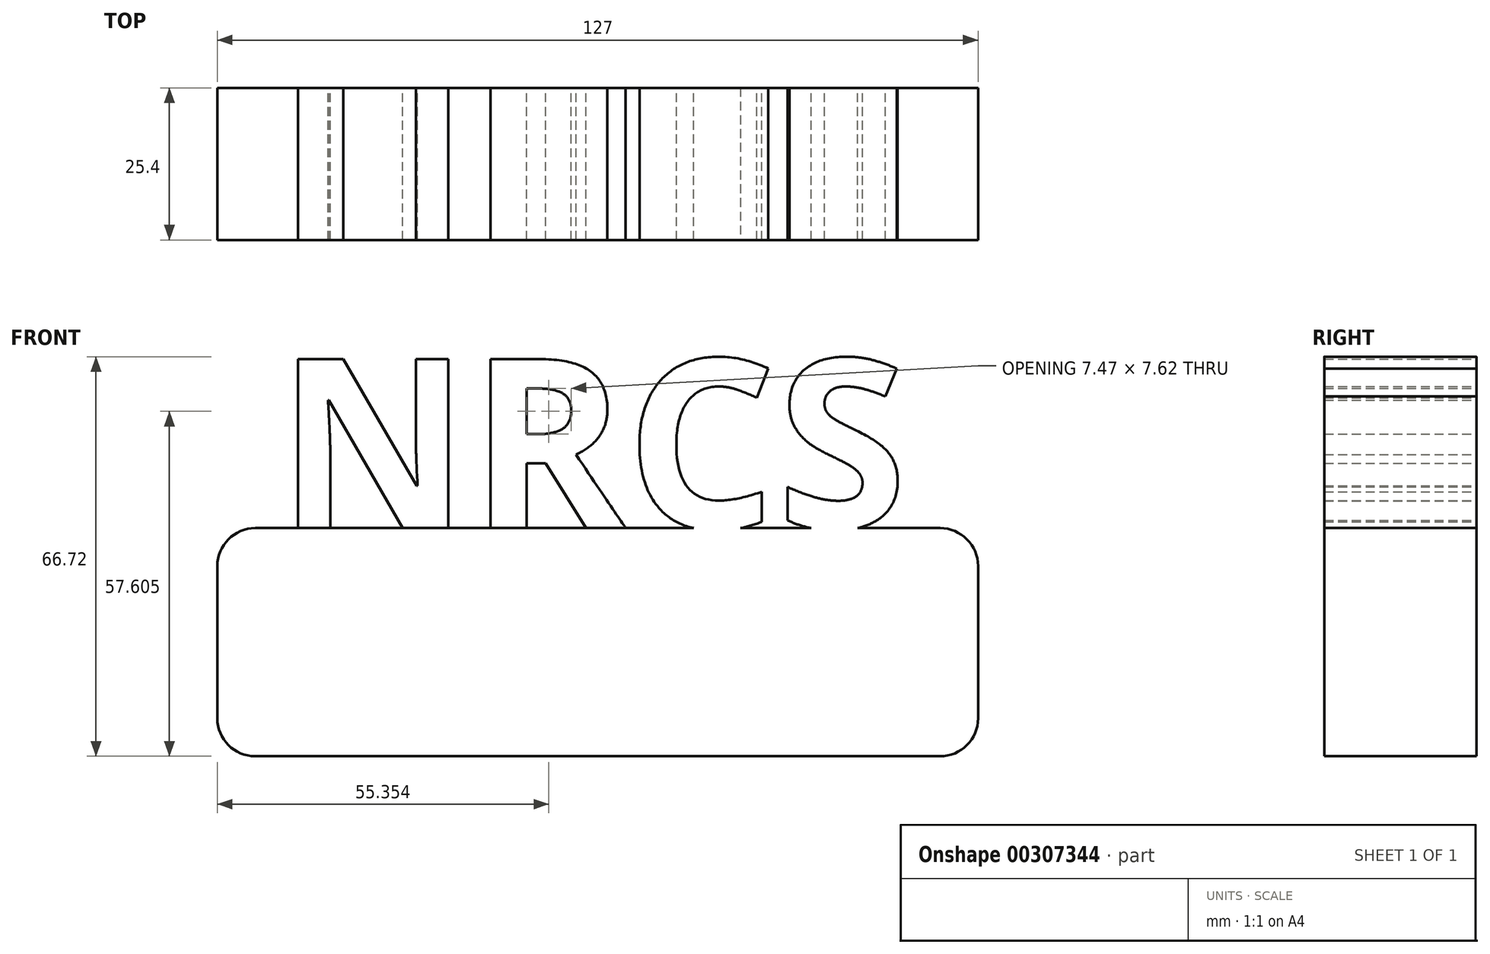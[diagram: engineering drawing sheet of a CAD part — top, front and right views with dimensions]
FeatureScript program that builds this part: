
annotation { "Feature Type Name" : "Feature", "Feature Type Description" : "" }
export const myFeature = defineFeature(function(context is Context, id is Id, definition is map)
    precondition{}
    {
        {
            var Q0;
            Q0=qCreatedBy(makeId("Front.planeOp"),FACE);
            var sketch = newSketch(context, id + "F0", { "sketchPlane" : qUnion([Q0])});
            skLineSegment(sketch, "E0.bottom", {"start": v(-30.95, -16.86) * mm, "end": v(83.35, -16.86) * mm});
            skLineSegment(sketch, "E0.top", {"start": v(-30.95, 21.24) * mm, "end": v(83.35, 21.24) * mm});
            skLineSegment(sketch, "E0.left", {"start": v(-37.3, -10.51) * mm, "end": v(-37.3, 14.89) * mm});
            skLineSegment(sketch, "E0.right", {"start": v(89.7, -10.51) * mm, "end": v(89.7, 14.89) * mm});
            skArc(sketch, "E1.filletArc", {"start": v(-30.95, 21.24) * mm, "mid": v(-35.44, 19.38) * mm, "end": v(-37.3, 14.89) * mm});
            skArc(sketch, "E2.filletArc", {"start": v(-37.3, -10.51) * mm, "mid": v(-35.44, -15) * mm, "end": v(-30.95, -16.86) * mm});
            skArc(sketch, "E3.filletArc", {"start": v(83.35, -16.86) * mm, "mid": v(87.84, -15) * mm, "end": v(89.7, -10.51) * mm});
            skArc(sketch, "E4.filletArc", {"start": v(89.7, 14.89) * mm, "mid": v(87.84, 19.38) * mm, "end": v(83.35, 21.24) * mm});
            skText(sketch, "E5", { "text": "NRCS", "fontName": "OpenSans-Bold.ttf"});
            const initialGuessF0  = {"E5": [-0.02735, 0.02124, 1, 0, 0.02846]};
            skSetInitialGuess(sketch, initialGuessF0);
            skSolve(sketch);
        }
        {
            var Q0;
            Q0 = qSketchRegion(id + "F0", true);
            extrude(context, id + "F1", {"entities" : qUnion([Q0]), "depth" : 25.4 * mm});
        }
    });
